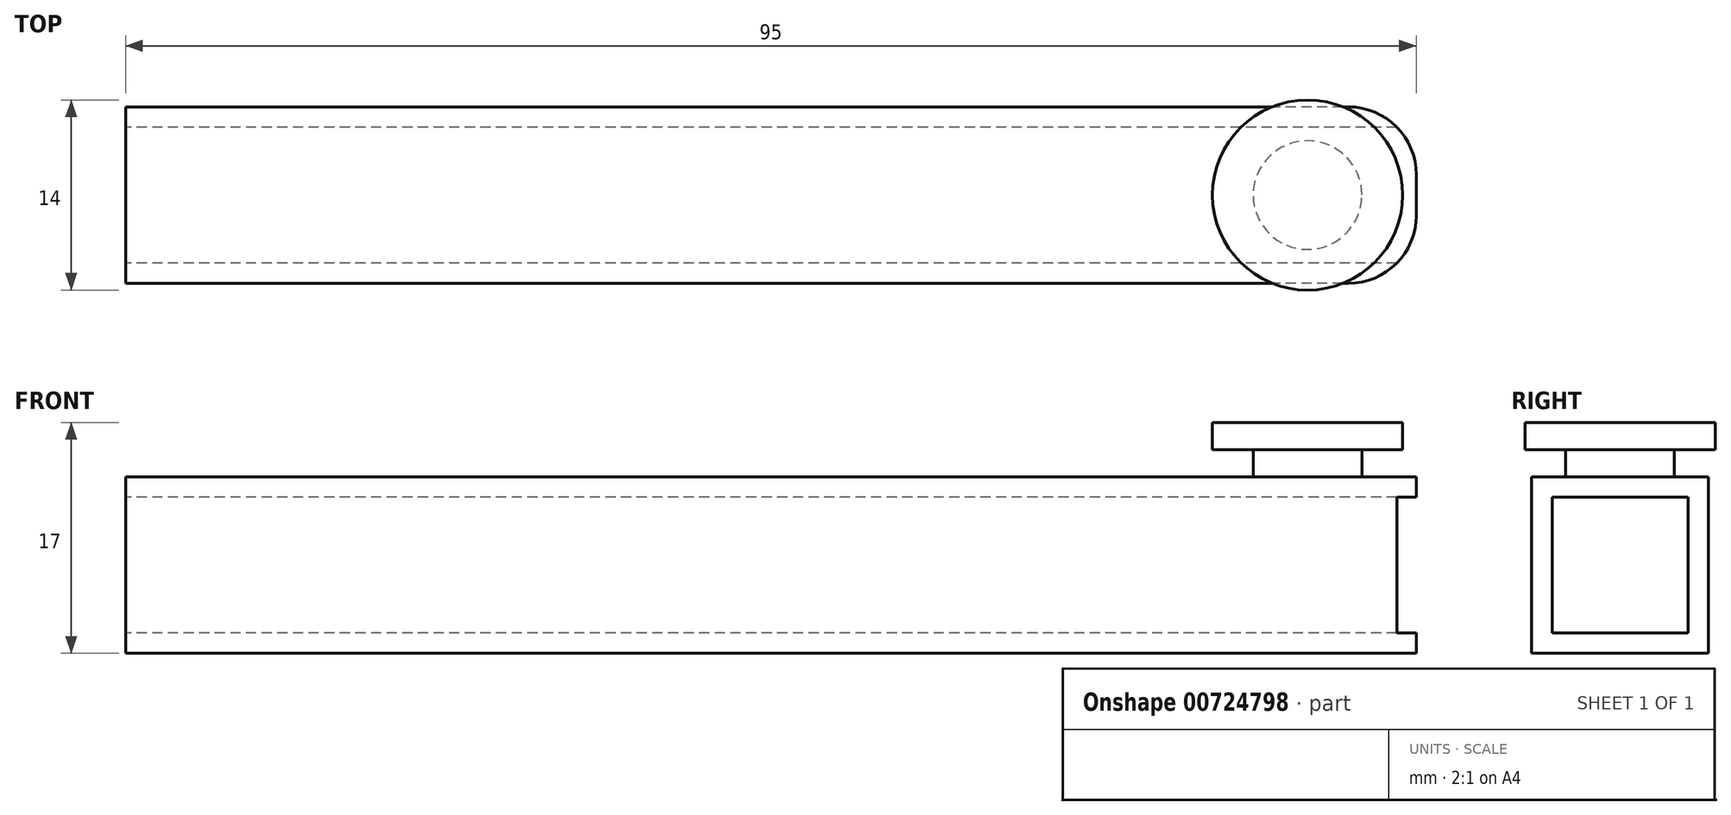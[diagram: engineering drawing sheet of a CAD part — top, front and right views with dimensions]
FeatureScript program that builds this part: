
annotation { "Feature Type Name" : "Feature", "Feature Type Description" : "" }
export const myFeature = defineFeature(function(context is Context, id is Id, definition is map)
    precondition{}
    {
        {
            var Q0;
            Q0=qCreatedBy(makeId("Right.planeOp"),FACE);
            var sketch = newSketch(context, id + "F0", { "sketchPlane" : qUnion([Q0])});
            skLineSegment(sketch, "E0.bottom", {"start": v(-5.75, 0) * mm, "end": v(-18.75, 0) * mm});
            skLineSegment(sketch, "E0.top", {"start": v(-5.75, 13) * mm, "end": v(-18.75, 13) * mm});
            skLineSegment(sketch, "E0.left", {"start": v(-5.75, 0) * mm, "end": v(-5.75, 13) * mm});
            skLineSegment(sketch, "E0.right", {"start": v(-18.75, 0) * mm, "end": v(-18.75, 13) * mm});
            skLineSegment(sketch, "E1.bottom", {"start": v(-17.25, 11.5) * mm, "end": v(-7.25, 11.5) * mm});
            skLineSegment(sketch, "E1.top", {"start": v(-17.25, 1.5) * mm, "end": v(-7.25, 1.5) * mm});
            skLineSegment(sketch, "E1.left", {"start": v(-17.25, 11.5) * mm, "end": v(-17.25, 1.5) * mm});
            skLineSegment(sketch, "E1.right", {"start": v(-7.25, 11.5) * mm, "end": v(-7.25, 1.5) * mm});
            skLineSegment(sketch, "E2", {"start": v(-7.25, 6.5) * mm, "end": v(-5.75, 6.5) * mm, "construction": true});
            skLineSegment(sketch, "E3", {"start": v(-12.25, 11.5) * mm, "end": v(-12.25, 13) * mm, "construction": true});
            skSolve(sketch);
        }
        {
            var Q0;
            Q0 = qSketchRegion(id + "F0", true);
            extrude(context, id + "F1", {"entities" : qUnion([Q0]), "depth" : 95 * mm, "offsetDistance" : 25 * mm});
        }
        {
            var Q0;
            Q0=makeQuery(id+"F1.opExtrude","CAP_EDGE",EDGE,{"disambiguationData":[OSD([sQuery(id+"F0.wireOp",EDGE,"E0.left")])],"isStart":false});
            var Q1;
            Q1=makeQuery(id+"F1.opExtrude","CAP_EDGE",EDGE,{"disambiguationData":[OSD([sQuery(id+"F0.wireOp",EDGE,"E0.right")])],"isStart":false});
            fillet(context, id + "F2", {"entities" : qUnion([Q0, Q1]), "radius" : 5 * mm, "tangentPropagation" : true, "allowEdgeOverflow" : false});
        }
        {
            var Q0;
            Q0=makeQuery(id+"F1.opExtrude","SWEPT_FACE",FACE,{"disambiguationData":[OSD([sQuery(id+"F0.wireOp",EDGE,"E0.top")])]});
            var sketch = newSketch(context, id + "F3", { "sketchPlane" : qUnion([Q0])});
            skLineSegment(sketch, "E4", {"start": v(95, -12.25) * mm, "end": v(87, -12.25) * mm, "construction": true});
            skCircle(sketch, "E5", {"center": v(87, -12.25) * mm, "radius": 4 * mm});
            skSolve(sketch);
        }
        {
            var Q0;
            Q0=makeQuery(id+"F3.imprint","IMPRINT",FACE,{"disambiguationData":[TD([[makeQuery(id+"F3.imprint","IMPRINT",EDGE,{"derivedFrom":sQuery(id+"F3.wireOp",EDGE,"E5")}),1.0]])]});
            extrude(context, id + "F4", {"entities" : qUnion([Q0]), "operationType" : NewBodyOperationType.ADD, "depth" : 2 * mm, "offsetDistance" : 25 * mm});
        }
        {
            var Q0;
            Q0=makeQuery(id+"F4.opExtrude","CAP_FACE",FACE,{"disambiguationData":[OSD([sQuery(id+"F3.wireOp",EDGE,"E5")])],"isStart":false});
            var sketch = newSketch(context, id + "F5", { "sketchPlane" : qUnion([Q0])});
            skCircle(sketch, "E6", {"center": v(87, -12.25) * mm, "radius": 7 * mm});
            skSolve(sketch);
        }
        {
            var Q0;
            Q0=makeQuery(id+"F5.imprint","IMPRINT",FACE,{"disambiguationData":[TD([[makeQuery(id+"F5.imprint","IMPRINT",EDGE,{"derivedFrom":sQuery(id+"F5.wireOp",EDGE,"E6")}),1.0]])]});
            var Q1;
            Q1=makeQuery(id+"F5.imprint","IMPRINT",FACE,{"disambiguationData":[TD([[makeQuery(id+"F5.imprint","IMPRINT",EDGE,{"derivedFrom":makeQuery(id+"F4.opExtrude","CAP_EDGE",EDGE,{"disambiguationData":[OSD([sQuery(id+"F3.wireOp",EDGE,"E5")])],"isStart":false})}),1.0]])]});
            extrude(context, id + "F6", {"entities" : qUnion([Q0, Q1]), "operationType" : NewBodyOperationType.ADD, "depth" : 2 * mm, "offsetDistance" : 25 * mm});
        }
    });
